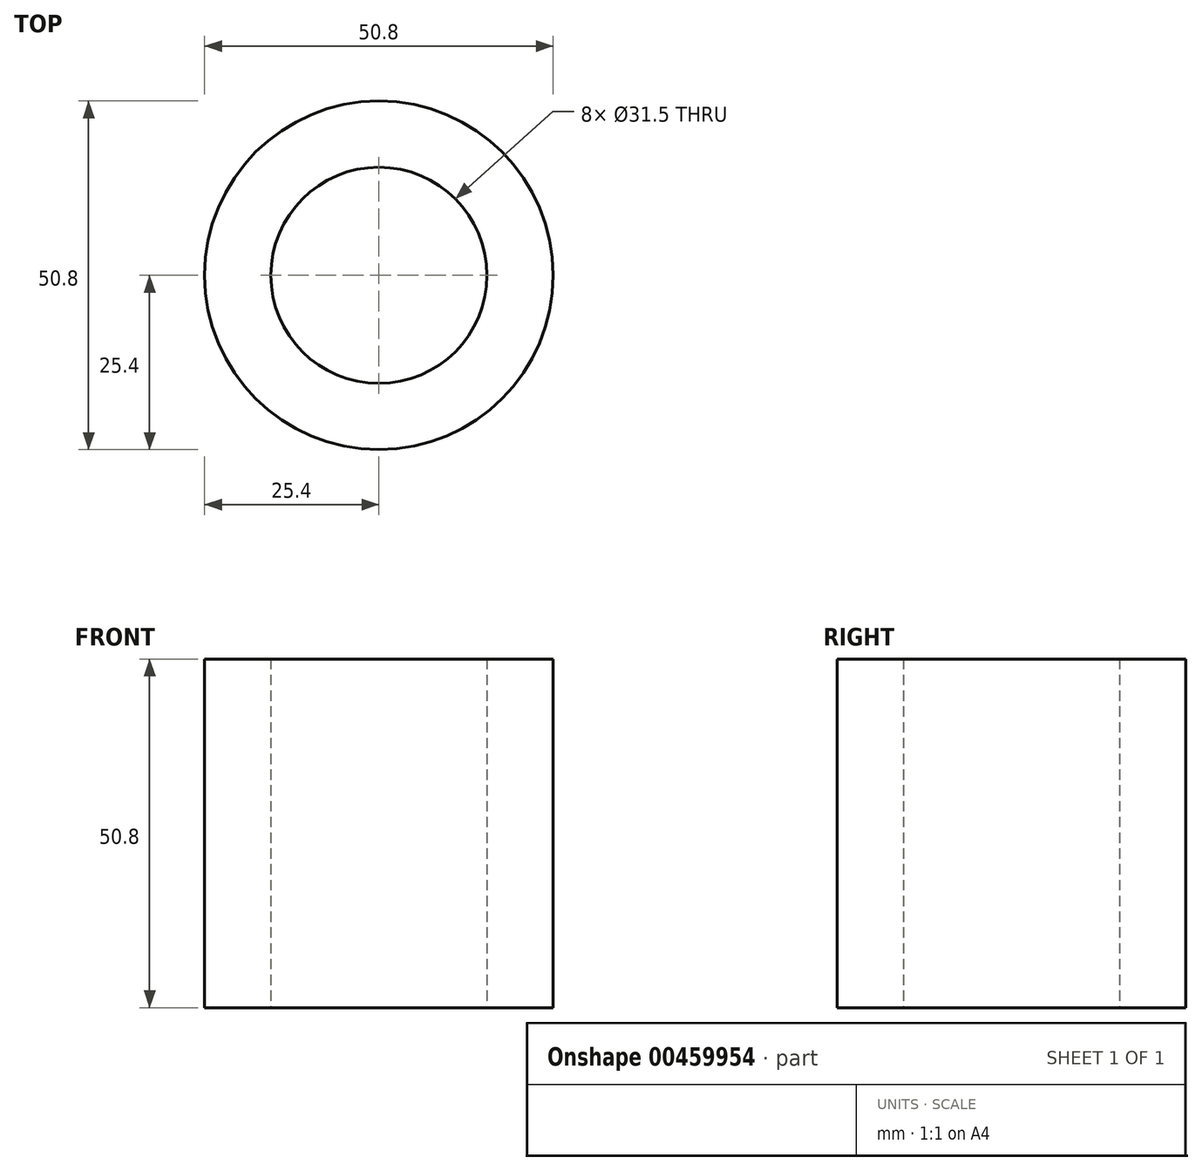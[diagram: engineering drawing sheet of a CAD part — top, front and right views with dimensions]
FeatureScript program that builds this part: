
annotation { "Feature Type Name" : "Feature", "Feature Type Description" : "" }
export const myFeature = defineFeature(function(context is Context, id is Id, definition is map)
    precondition{}
    {
        {
            var Q0;
            Q0=qCreatedBy(makeId("Top.planeOp"),FACE);
            var sketch = newSketch(context, id + "F0", { "sketchPlane" : qUnion([Q0])});
            skCircle(sketch, "E0", {"center": v(0, 0) * mm, "radius": 15.75 * mm});
            skCircle(sketch, "E1", {"center": v(0, 0) * mm, "radius": 25.4 * mm});
            skSolve(sketch);
        }
        {
            var Q0;
            Q0=makeQuery(id+"F0.imprint","IMPRINT",FACE,{"disambiguationData":[TD([[makeQuery(id+"F0.imprint","IMPRINT",EDGE,{"derivedFrom":sQuery(id+"F0.wireOp",EDGE,"E0")}),-1.0]])]});
            extrude(context, id + "F1", {"entities" : qUnion([Q0]), "depth" : 50.8 * mm});
        }
    });
